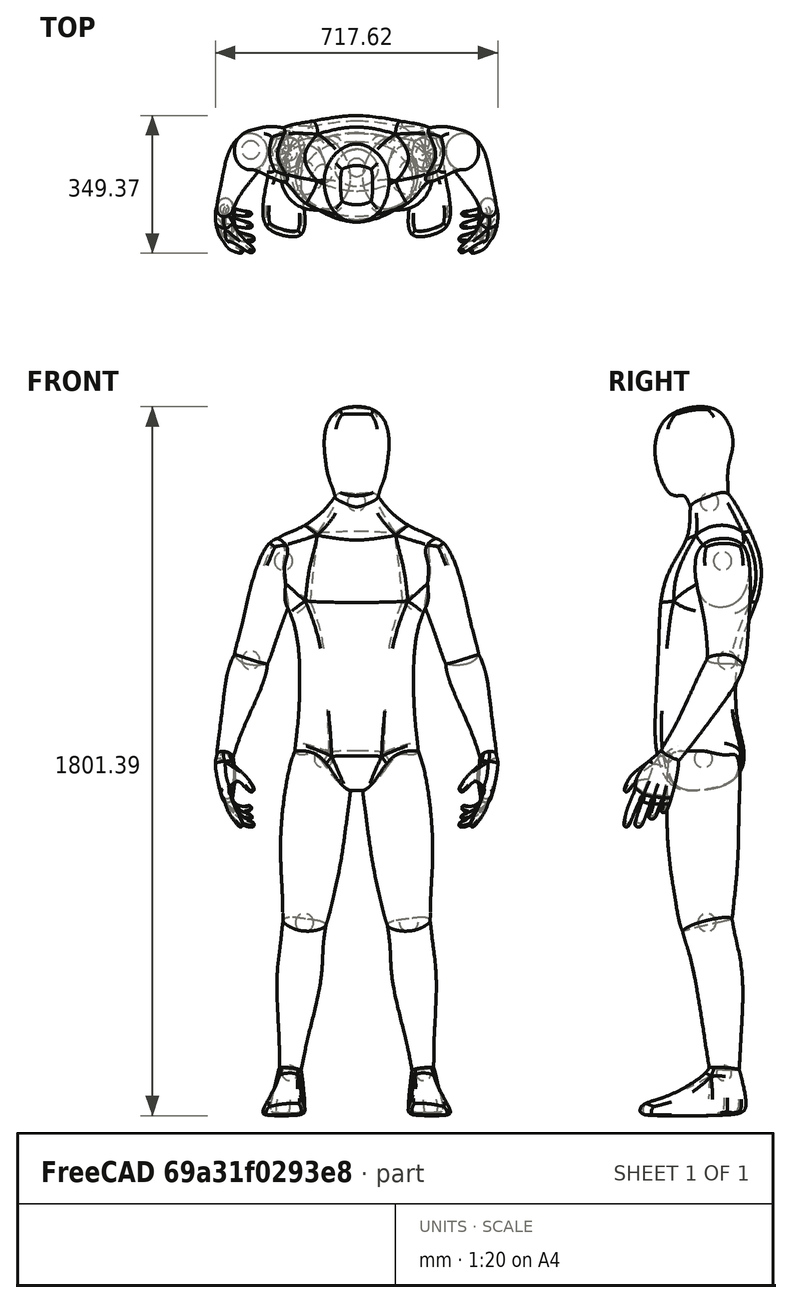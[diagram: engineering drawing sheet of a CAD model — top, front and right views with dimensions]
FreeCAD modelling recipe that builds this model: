
FCSTD DOCUMENT  (FreeCAD 1.0R39109 (Git))
Label: HumanModel
License: All rights reserved
LicenseURL: https://en.wikipedia.org/wiki/All_rights_reserved
objects: Part::Feature×14, Part::MultiFuse×7, App::Part×1
note: 21 computed .brp shape members not serialized (recipe doc carries the construction recipe); baked Part::Feature solids carry a one-line shape summary decoded from their .brp

FEATURE [Part::Feature] Part__Feature  label="HUMAN"
  shape: bbox 164.7 x 199.3 x 290.8 mm, 78 faces (baked)
FEATURE [Part::Feature] Part__Feature001  label="HUMAN001"
  shape: bbox 476.9 x 270.3 x 775.9 mm, 218 faces (baked)
FEATURE [Part::Feature] Part__Feature002  label="HUMAN002"
  shape: bbox 179.1 x 141.6 x 352.4 mm, 80 faces (baked)
FEATURE [Part::Feature] Part__Feature003  label="HUMAN003"
  shape: bbox 128.5 x 218.9 x 311.6 mm, 100 faces (baked)
FEATURE [Part::Feature] Part__Feature004  label="HUMAN004"
  shape: bbox 99.16 x 139.8 x 204.2 mm, 167 faces (baked)
FEATURE [Part::Feature] Part__Feature005  label="HUMAN005"
  shape: bbox 181.6 x 186.2 x 536.4 mm, 100 faces (baked)
FEATURE [Part::Feature] Part__Feature006  label="HUMAN006"
  shape: bbox 124.6 x 156.1 x 457.2 mm, 100 faces (baked)
FEATURE [Part::Feature] Part__Feature007  label="HUMAN007"
  shape: bbox 107.7 x 269.7 x 134.5 mm, 82 faces (baked)
FEATURE [Part::Feature] Part__Feature008  label="HUMAN008"
  shape: bbox 179.1 x 141.6 x 352.4 mm, 80 faces (baked)
FEATURE [Part::Feature] Part__Feature009  label="HUMAN009"
  shape: bbox 128.5 x 218.9 x 311.6 mm, 100 faces (baked)
FEATURE [Part::Feature] Part__Feature010  label="HUMAN010"
  shape: bbox 99.16 x 139.8 x 204.2 mm, 167 faces (baked)
FEATURE [Part::Feature] Part__Feature011  label="HUMAN011"
  shape: bbox 181.6 x 186.2 x 536.4 mm, 100 faces (baked)
FEATURE [Part::Feature] Part__Feature012  label="HUMAN012"
  shape: bbox 124.6 x 156.1 x 457.2 mm, 100 faces (baked)
FEATURE [Part::Feature] Part__Feature013  label="HUMAN013"
  shape: bbox 107.7 x 269.7 x 134.5 mm, 82 faces (baked)
FEATURE [Part::MultiFuse] Fusion
  Refine = true
  Shapes = -> [Part__Feature001,Part__Feature]
FEATURE [Part::MultiFuse] Fusion001
  Refine = true
  Shapes = -> [Part__Feature002,Part__Feature003,Part__Feature004]
FEATURE [Part::MultiFuse] Fusion002
  Refine = true
  Shapes = -> [Part__Feature005,Part__Feature006,Part__Feature007]
FEATURE [Part::MultiFuse] Fusion003
  Refine = true
  Shapes = -> [Part__Feature008,Part__Feature009,Part__Feature010]
FEATURE [Part::MultiFuse] Fusion004
  Refine = true
  Shapes = -> [Part__Feature011,Part__Feature012,Part__Feature013]
FEATURE [Part::MultiFuse] Fusion005
  Refine = true
  Shapes = -> [Fusion,Fusion001,Fusion002]
FEATURE [Part::MultiFuse] Fusion006
  Refine = true
  Shapes = -> [Fusion005,Fusion003,Fusion004]
FEATURE [App::Part] Part
  Group = -> [Fusion001,Fusion,Fusion003,Fusion002,Part__Feature009,Part__Feature001,Part__Feature008,Part__Feature004,Part__Feature002,Part__Feature006,Part__Feature005,Fusion004,Part__Feature012,Part__Feature,Part__Feature007,Part__Feature013,Part__Feature010,Fusion005,Part__Feature003,Part__Feature011,Fusion006]
  Origin = -> Origin001
